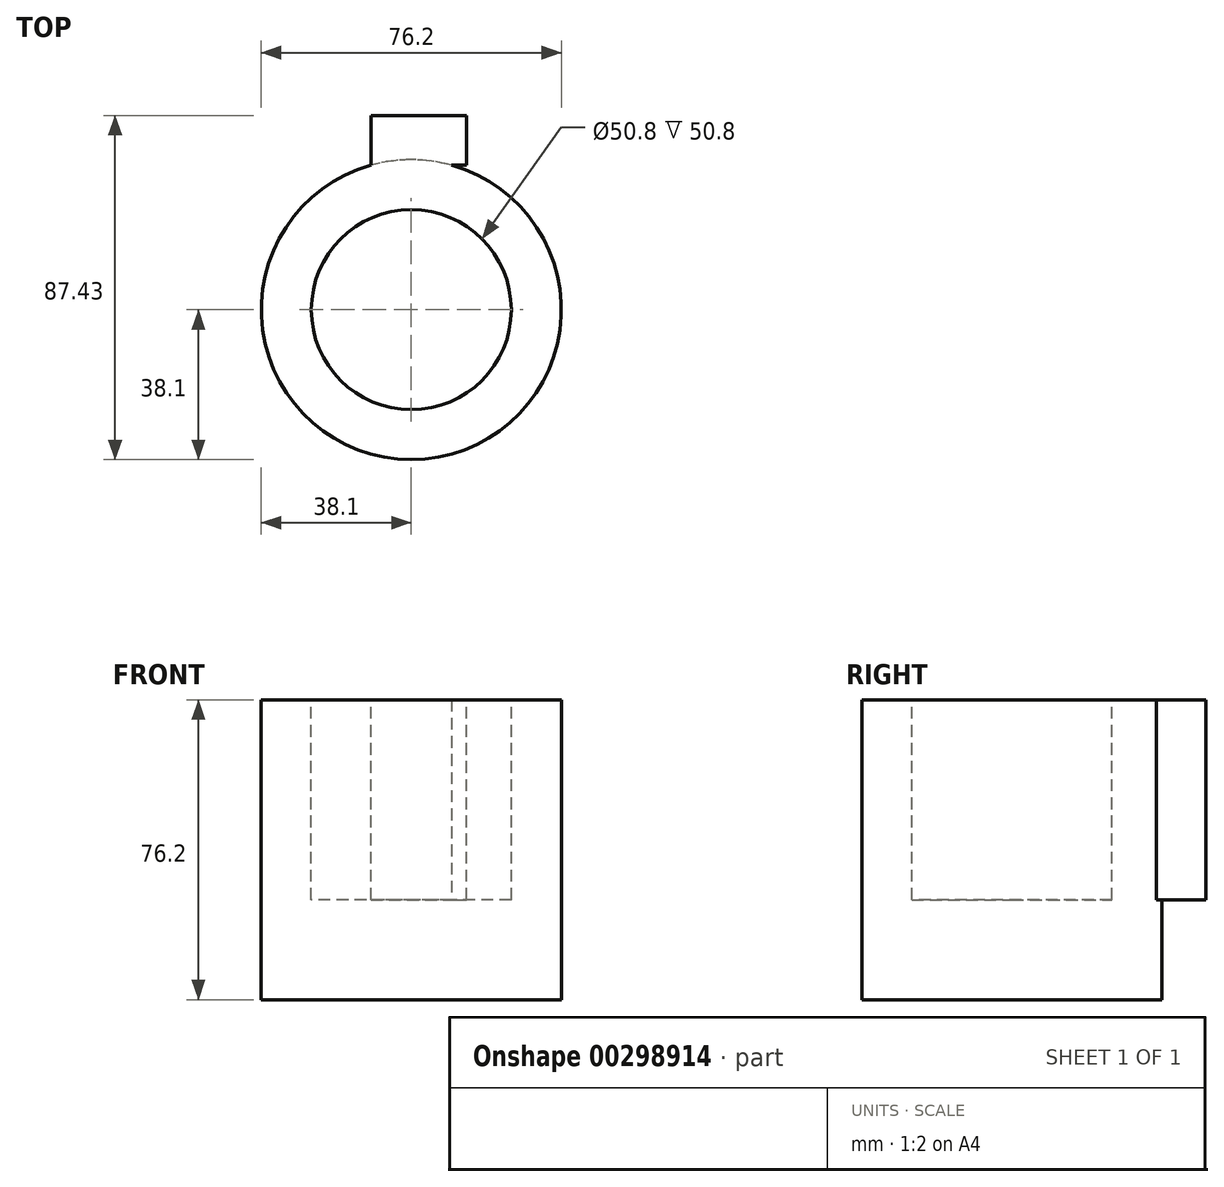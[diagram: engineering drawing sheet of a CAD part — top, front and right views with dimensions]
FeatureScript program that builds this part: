
annotation { "Feature Type Name" : "Feature", "Feature Type Description" : "" }
export const myFeature = defineFeature(function(context is Context, id is Id, definition is map)
    precondition{}
    {
        {
            var Q0;
            Q0=qCreatedBy(makeId("Top.planeOp"),FACE);
            var sketch = newSketch(context, id + "F0", { "sketchPlane" : qUnion([Q0])});
            skCircle(sketch, "E0", {"center": v(0, 0) * mm, "radius": 38.1 * mm});
            skSolve(sketch);
        }
        {
            var Q0;
            Q0 = qSketchRegion(id + "F0", true);
            extrude(context, id + "F1", {"entities" : qUnion([Q0]), "depth" : 76.2 * mm});
        }
        {
            var Q0;
            Q0=makeQuery(id+"F1.opExtrude","CAP_FACE",FACE,{"disambiguationData":[OSD([sQuery(id+"F0.wireOp",EDGE,"E0")])],"isStart":false});
            var sketch = newSketch(context, id + "F2", { "sketchPlane" : qUnion([Q0])});
            skCircle(sketch, "E1", {"center": v(0, 0) * mm, "radius": 25.4 * mm});
            skSolve(sketch);
        }
        {
            var Q0;
            Q0 = qSketchRegion(id + "F2", true);
            extrude(context, id + "F3", {"entities" : qUnion([Q0]), "operationType" : NewBodyOperationType.REMOVE, "oppositeDirection" : true, "depth" : 50.8 * mm});
        }
        {
            var Q0;
            Q0=makeQuery(id+"F1.opExtrude","CAP_FACE",FACE,{"disambiguationData":[OSD([sQuery(id+"F0.wireOp",EDGE,"E0")])],"isStart":false});
            var sketch = newSketch(context, id + "F4", { "sketchPlane" : qUnion([Q0])});
            skLineSegment(sketch, "E2.bottom", {"start": v(-10.28, 36.69) * mm, "end": v(13.99, 36.69) * mm});
            skLineSegment(sketch, "E2.top", {"start": v(-10.28, 49.33) * mm, "end": v(13.99, 49.33) * mm});
            skLineSegment(sketch, "E2.left", {"start": v(-10.28, 36.69) * mm, "end": v(-10.28, 49.33) * mm});
            skLineSegment(sketch, "E2.right", {"start": v(13.99, 36.69) * mm, "end": v(13.99, 49.33) * mm});
            skSolve(sketch);
        }
        {
            var Q0;
            Q0 = qSketchRegion(id + "F4", true);
            extrude(context, id + "F5", {"entities" : qUnion([Q0]), "operationType" : NewBodyOperationType.ADD, "oppositeDirection" : true, "depth" : 50.8 * mm});
        }
    });
